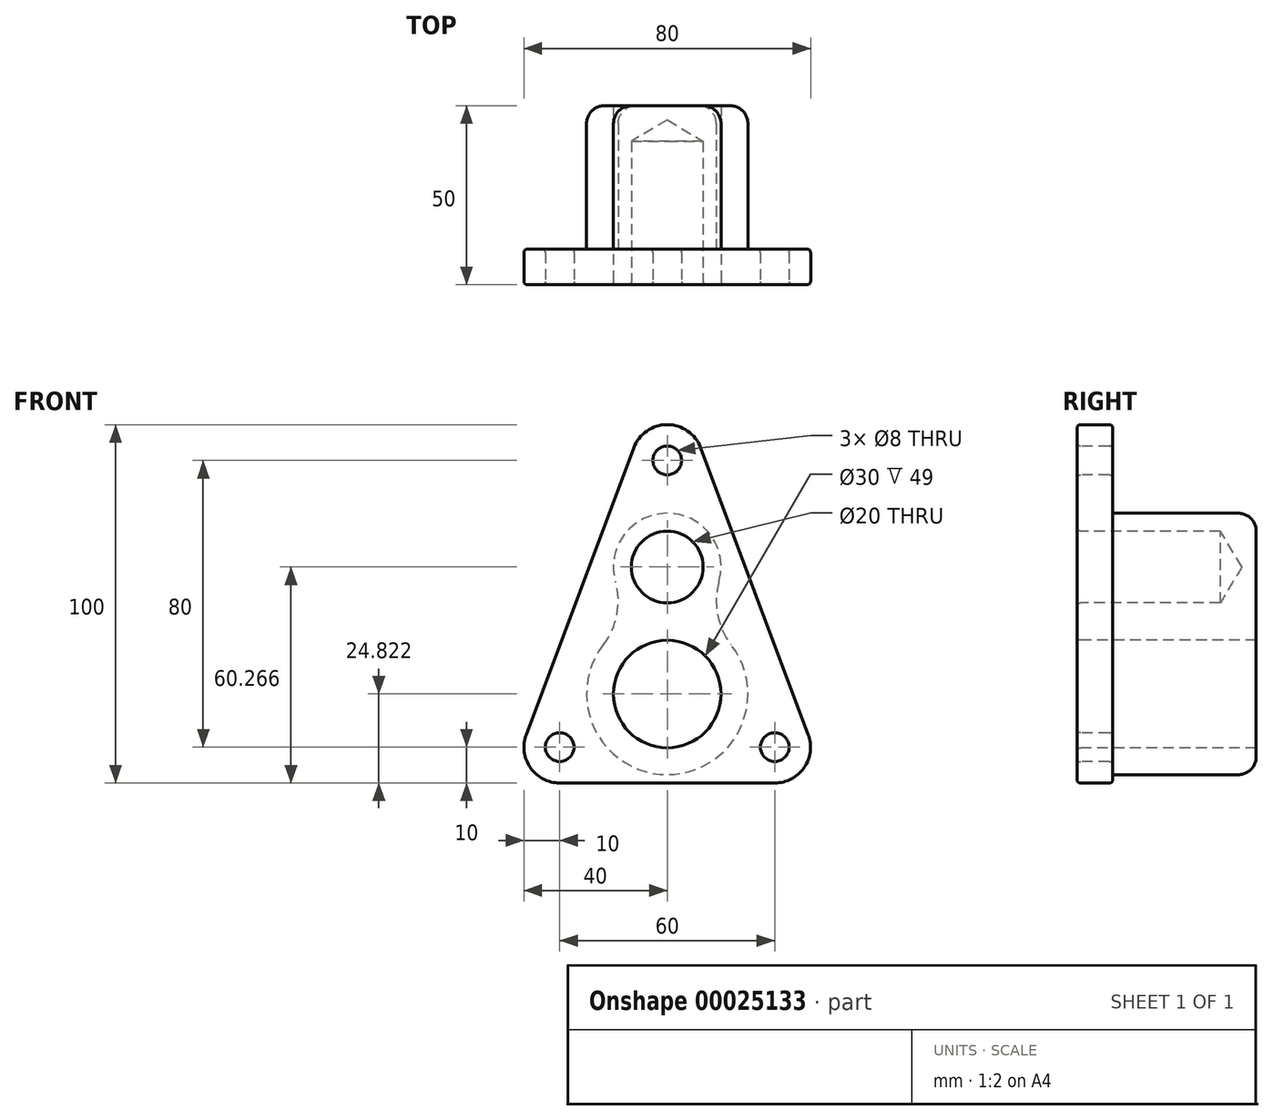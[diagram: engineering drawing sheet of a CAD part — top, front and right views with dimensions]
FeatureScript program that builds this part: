
annotation { "Feature Type Name" : "Feature", "Feature Type Description" : "" }
export const myFeature = defineFeature(function(context is Context, id is Id, definition is map)
    precondition{}
    {
        {
            var Q0;
            Q0=qCreatedBy(makeId("Front.planeOp"),FACE);
            var sketch = newSketch(context, id + "F0", { "sketchPlane" : qUnion([Q0])});
            skCircle(sketch, "E0", {"center": v(-30, 0) * mm, "radius": 10 * mm});
            skCircle(sketch, "E1", {"center": v(30, 0) * mm, "radius": 10 * mm});
            skCircle(sketch, "E2", {"center": v(0, 80) * mm, "radius": 10 * mm});
            skLineSegment(sketch, "E3", {"start": v(-39.36, 3.51) * mm, "end": v(-9.36, 83.51) * mm});
            skLineSegment(sketch, "E4.MirrorCS", {"start": v(39.36, 3.51) * mm, "end": v(9.36, 83.51) * mm});
            skLineSegment(sketch, "E5", {"start": v(-30, -10) * mm, "end": v(30, -10) * mm});
            skCircle(sketch, "E6", {"center": v(0, 80) * mm, "radius": 4 * mm});
            skCircle(sketch, "E7", {"center": v(30, 0) * mm, "radius": 4 * mm});
            skCircle(sketch, "E8", {"center": v(-30, 0) * mm, "radius": 4 * mm});
            skArc(sketch, "E9", {"start": v(-17.83, 28.54) * mm, "mid": v(0, -7.68) * mm, "end": v(17.83, 28.54) * mm});
            skArc(sketch, "E10", {"start": v(14.43, 46.18) * mm, "mid": v(0, 65.27) * mm, "end": v(-14.43, 46.18) * mm});
            skPoint(sketch, "E11.visualSharp", {"position": v(-5.98, 36.51) * mm});
            skArc(sketch, "E11.filletArc", {"start": v(-17.83, 28.54) * mm, "mid": v(-14.04, 36.96) * mm, "end": v(-14.43, 46.18) * mm});
            skPoint(sketch, "E12.visualSharp", {"position": v(5.98, 36.51) * mm});
            skArc(sketch, "E12.filletArc", {"start": v(14.43, 46.18) * mm, "mid": v(14.04, 36.96) * mm, "end": v(17.83, 28.54) * mm});
            skSolve(sketch);
        }
        {
            var Q0;
            Q0=makeQuery(id+"F0.imprint","IMPRINT",FACE,{"disambiguationData":[TD([[makeQuery(id+"F0.imprint","IMPRINT",EDGE,{"derivedFrom":sQuery(id+"F0.wireOp",EDGE,"E8")}),-1.0]])]});
            var Q1;
            Q1=makeQuery(id+"F0.imprint","IMPRINT",FACE,{"disambiguationData":[TD([[makeQuery(id+"F0.imprint","IMPRINT",EDGE,{"derivedFrom":sQuery(id+"F0.wireOp",EDGE,"E6")}),-1.0]])]});
            var Q2;
            {var subQ2=sQuery(id+"F0.wireOp",EDGE,"E3");Q2=makeQuery(id+"F0.imprint","IMPRINT",FACE,{"disambiguationData":[TD([[makeQuery(id+"F0.imprint","IMPRINT",EDGE,{"derivedFrom":subQ2}),-1.0]])]});}
            var Q3;
            Q3=makeQuery(id+"F0.imprint","IMPRINT",FACE,{"disambiguationData":[TD([[makeQuery(id+"F0.imprint","IMPRINT",EDGE,{"derivedFrom":sQuery(id+"F0.wireOp",EDGE,"E7")}),-1.0]])]});
            extrude(context, id + "F1", {"entities" : qUnion([Q0, Q1, Q2, Q3]), "oppositeDirection" : true, "depth" : 10 * mm});
        }
        {
            var Q0;
            Q0=makeQuery(id+"F0.imprint","IMPRINT",FACE,{"disambiguationData":[TD([[makeQuery(id+"F0.imprint","IMPRINT",EDGE,{"derivedFrom":sQuery(id+"F0.wireOp",EDGE,"E9")}),1.0]])]});
            extrude(context, id + "F2", {"entities" : qUnion([Q0]), "operationType" : NewBodyOperationType.ADD, "oppositeDirection" : true, "depth" : 50 * mm});
        }
        {
            var Q0;
            Q0=sQuery(id+"F0.wireOp",VERTEX,"E9.center");
            var Q1;
            Q1=makeQuery(id+"F1.opExtrude","SWEPT_BODY",BODY,{"disambiguationData":[OSD([sQuery(id+"F0.wireOp",EDGE,"E0"),sQuery(id+"F0.wireOp",EDGE,"E1"),sQuery(id+"F0.wireOp",EDGE,"E2"),sQuery(id+"F0.wireOp",EDGE,"E3"),sQuery(id+"F0.wireOp",EDGE,"E4.MirrorCS"),sQuery(id+"F0.wireOp",EDGE,"E5"),sQuery(id+"F0.wireOp",EDGE,"E6"),sQuery(id+"F0.wireOp",EDGE,"E7"),sQuery(id+"F0.wireOp",EDGE,"E8"),sQuery(id+"F0.wireOp",EDGE,"E9"),sQuery(id+"F0.wireOp",EDGE,"E10"),sQuery(id+"F0.wireOp",EDGE,"E11.filletArc"),sQuery(id+"F0.wireOp",EDGE,"E12.filletArc")])]});
            hole(context, id + "F3", {"style" : HoleStyle.SIMPLE, "holeDiameter" : 30 * mm, "endStyle" : HoleEndStyle.THROUGH, "locations" : qUnion([Q0]), "scope" : qUnion([Q1])});
        }
        {
            var Q0;
            Q0=sQuery(id+"F0.wireOp",VERTEX,"E10.center");
            var Q1;
            Q1=makeQuery(id+"F1.opExtrude","SWEPT_BODY",BODY,{"disambiguationData":[OSD([sQuery(id+"F0.wireOp",EDGE,"E0"),sQuery(id+"F0.wireOp",EDGE,"E1"),sQuery(id+"F0.wireOp",EDGE,"E2"),sQuery(id+"F0.wireOp",EDGE,"E3"),sQuery(id+"F0.wireOp",EDGE,"E4.MirrorCS"),sQuery(id+"F0.wireOp",EDGE,"E5"),sQuery(id+"F0.wireOp",EDGE,"E6"),sQuery(id+"F0.wireOp",EDGE,"E7"),sQuery(id+"F0.wireOp",EDGE,"E8"),sQuery(id+"F0.wireOp",EDGE,"E9"),sQuery(id+"F0.wireOp",EDGE,"E10"),sQuery(id+"F0.wireOp",EDGE,"E11.filletArc"),sQuery(id+"F0.wireOp",EDGE,"E12.filletArc")])]});
            hole(context, id + "F4", {"style" : HoleStyle.SIMPLE, "holeDiameter" : 20 * mm, "endStyle" : HoleEndStyle.BLIND, "holeDepth" : 40 * mm, "locations" : qUnion([Q0]), "scope" : qUnion([Q1])});
        }
        {
            var Q0;
            Q0=makeQuery(id+"F2.opExtrude","CAP_EDGE",EDGE,{"disambiguationData":[OSD([sQuery(id+"F0.wireOp",EDGE,"E12.filletArc")])],"isStart":false});
            fillet(context, id + "F5", {"entities" : qUnion([Q0]), "radius" : 5 * mm, "tangentPropagation" : true, "allowEdgeOverflow" : false});
        }
        {
            var Q0;
            Q0=makeQuery(id+"FoD63ZaUyHSXzbR_0.opExtrude","CAP_FACE",FACE,{"disambiguationData":[OSD([sQuery(id+"F0.wireOp",EDGE,"E1"),sQuery(id+"F0.wireOp",EDGE,"E7")])],"isStart":false});
            var Q1;
            Q1=makeQuery(id+"FoD63ZaUyHSXzbR_0.opExtrude","CAP_FACE",FACE,{"disambiguationData":[OSD([sQuery(id+"F0.wireOp",EDGE,"E0"),sQuery(id+"F0.wireOp",EDGE,"E8")])],"isStart":false});
            var Q2;
            Q2=makeQuery(id+"FoD63ZaUyHSXzbR_0.opExtrude","CAP_FACE",FACE,{"disambiguationData":[OSD([sQuery(id+"F0.wireOp",EDGE,"E2"),sQuery(id+"F0.wireOp",EDGE,"E6")])],"isStart":false});
            var Q3;
            Q3=makeQuery(id+"F1.opExtrude","CAP_EDGE",EDGE,{"disambiguationData":[OSD([sQuery(id+"F0.wireOp",EDGE,"E4.MirrorCS")])],"isStart":false});
            var Q4;
            Q4=makeQuery(id+"F1.opExtrude","CAP_EDGE",EDGE,{"disambiguationData":[OSD([sQuery(id+"F0.wireOp",EDGE,"E3")])],"isStart":false});
            var Q5;
            Q5=makeQuery(id+"F1.opExtrude","CAP_EDGE",EDGE,{"disambiguationData":[OSD([sQuery(id+"F0.wireOp",EDGE,"E5")])],"isStart":false});
            var Q6;
            Q6=makeQuery(id+"F3.hole-0.boolean.opBoolean","INTERSECT",EDGE,{"derivedFrom":[makeQuery(id+"F2.opExtrude","CAP_FACE",FACE,{"disambiguationData":[OSD([sQuery(id+"F0.wireOp",EDGE,"E9"),sQuery(id+"F0.wireOp",EDGE,"E10"),sQuery(id+"F0.wireOp",EDGE,"E11.filletArc"),sQuery(id+"F0.wireOp",EDGE,"E12.filletArc")])],"isStart":false}),makeQuery(id+"F3.hole-0.opRevolve","SWEPT_FACE",FACE,{"disambiguationData":[OSD([sQuery(id+"F3.hole-0.sketch.wireOp",EDGE,"core_line_2")])]})]});
            fillet(context, id + "F6", {"entities" : qUnion([Q0, Q1, Q2, Q3, Q4, Q5, Q6]), "radius" : 1 * mm, "tangentPropagation" : true, "allowEdgeOverflow" : false});
        }
        {
            var Q0;
            {var subQ0=sQuery(id+"F0.wireOp",EDGE,"E9");var subQ1=sQuery(id+"F0.wireOp",EDGE,"E10");var subQ2=sQuery(id+"F0.wireOp",EDGE,"E11.filletArc");var subQ3=sQuery(id+"F0.wireOp",EDGE,"E12.filletArc");Q0=makeQuery(id+"F2.boolean.opBoolean","MERGE",FACE,{"derivedFrom":[makeQuery(id+"F1.opExtrude","CAP_FACE",FACE,{"disambiguationData":[OSD([sQuery(id+"F0.wireOp",EDGE,"E0"),sQuery(id+"F0.wireOp",EDGE,"E1"),sQuery(id+"F0.wireOp",EDGE,"E2"),sQuery(id+"F0.wireOp",EDGE,"E3"),sQuery(id+"F0.wireOp",EDGE,"E4.MirrorCS"),sQuery(id+"F0.wireOp",EDGE,"E5"),sQuery(id+"F0.wireOp",EDGE,"E6"),sQuery(id+"F0.wireOp",EDGE,"E7"),sQuery(id+"F0.wireOp",EDGE,"E8"),subQ0,subQ1,subQ2,subQ3])],"isStart":true}),makeQuery(id+"F2.opExtrude","CAP_FACE",FACE,{"disambiguationData":[OSD([subQ0,subQ1,subQ2,subQ3])],"isStart":true})]});}
            fillet(context, id + "F7", {"entities" : qUnion([Q0]), "radius" : 1 * mm, "tangentPropagation" : true, "allowEdgeOverflow" : false});
        }
        {
            var Q0;
            Q0=makeQuery(id+"F1.opExtrude","CAP_EDGE",EDGE,{"disambiguationData":[OSD([sQuery(id+"F0.wireOp",EDGE,"E8")])],"isStart":false});
            var Q1;
            Q1=makeQuery(id+"F1.opExtrude","CAP_EDGE",EDGE,{"disambiguationData":[OSD([sQuery(id+"F0.wireOp",EDGE,"E7")])],"isStart":false});
            var Q2;
            Q2=makeQuery(id+"F1.opExtrude","CAP_EDGE",EDGE,{"disambiguationData":[OSD([sQuery(id+"F0.wireOp",EDGE,"E6")])],"isStart":false});
            fillet(context, id + "F8", {"entities" : qUnion([Q0, Q1, Q2]), "radius" : 1 * mm, "tangentPropagation" : true, "allowEdgeOverflow" : false});
        }
    });
